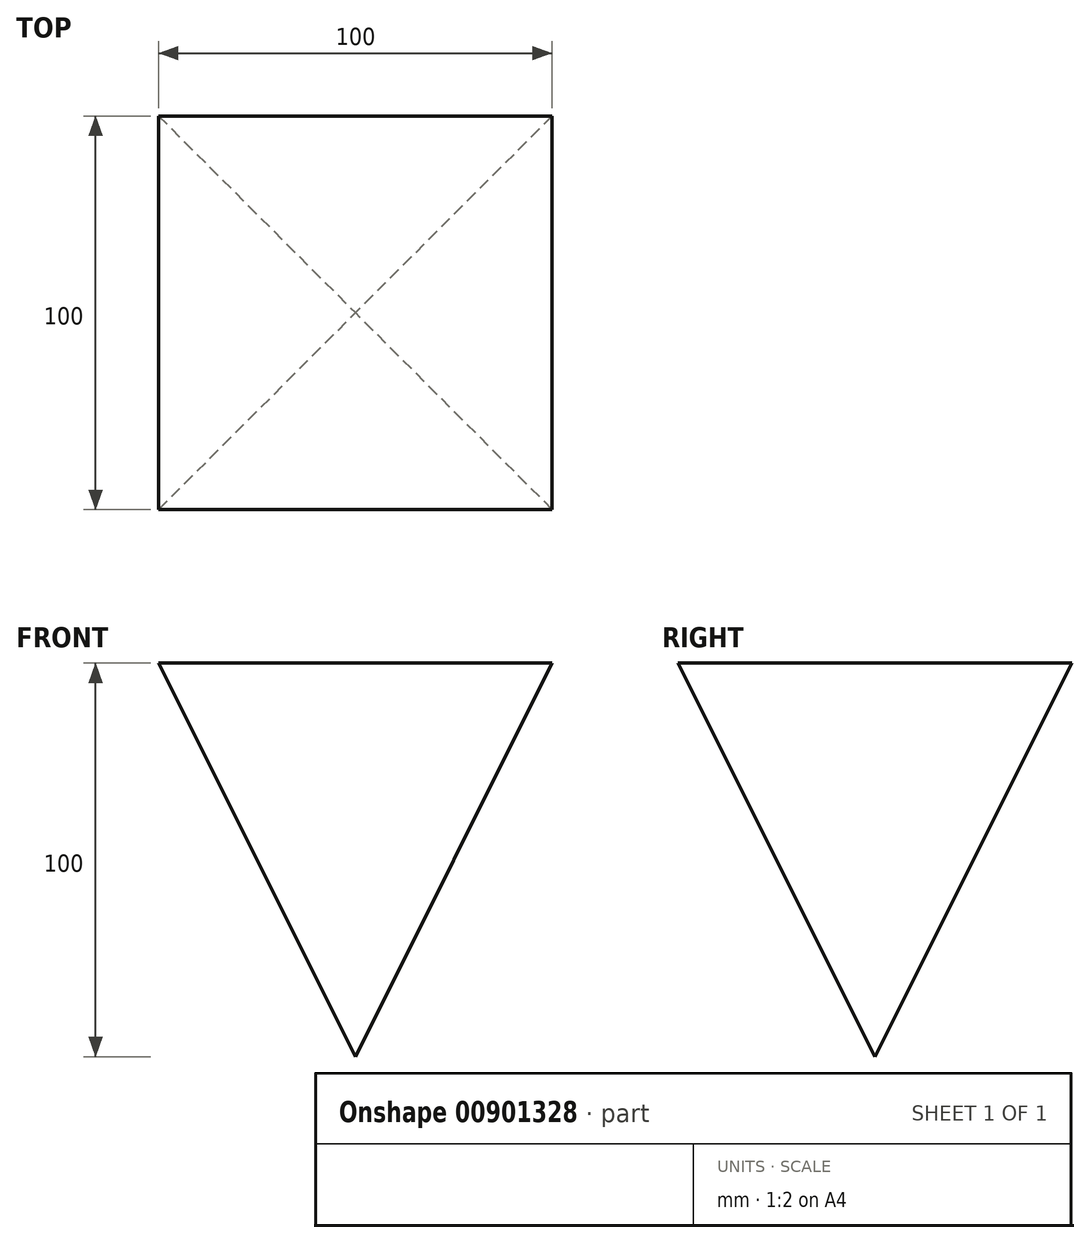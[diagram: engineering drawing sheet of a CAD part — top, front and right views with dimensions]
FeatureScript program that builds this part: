
annotation { "Feature Type Name" : "Feature", "Feature Type Description" : "" }
export const myFeature = defineFeature(function(context is Context, id is Id, definition is map)
    precondition{}
    {
        {
            var Q0;
            Q0=qCreatedBy(makeId("Top.planeOp"),FACE);
            var sketch = newSketch(context, id + "F0", { "sketchPlane" : qUnion([Q0])});
            skLineSegment(sketch, "E0.bottom", {"start": v(-50, 50) * mm, "end": v(50, 50) * mm});
            skLineSegment(sketch, "E0.top", {"start": v(-50, -50) * mm, "end": v(50, -50) * mm});
            skLineSegment(sketch, "E0.left", {"start": v(-50, 50) * mm, "end": v(-50, -50) * mm});
            skLineSegment(sketch, "E0.right", {"start": v(50, 50) * mm, "end": v(50, -50) * mm});
            skSolve(sketch);
        }
        {
            var Q0;
            Q0 = qSketchRegion(id + "F0", true);
            extrude(context, id + "F1", {"entities" : qUnion([Q0]), "endBound" : BoundingType.SYMMETRIC, "depth" : 100 * mm, "offsetDistance" : 25 * mm});
        }
        {
            var Q0;
            Q0=makeQuery(id+"F1.opExtrude","SWEPT_FACE",FACE,{"disambiguationData":[OSD([sQuery(id+"F0.wireOp",EDGE,"E0.right")])]});
            var sketch = newSketch(context, id + "F2", { "sketchPlane" : qUnion([Q0])});
            skLineSegment(sketch, "E1", {"start": v(50, 50) * mm, "end": v(0, -50) * mm});
            skLineSegment(sketch, "E2", {"start": v(-50, 50) * mm, "end": v(0, -50) * mm});
            skLineSegment(sketch, "E3", {"start": v(0, -50) * mm, "end": v(50, -50) * mm});
            skLineSegment(sketch, "E4", {"start": v(50, -50) * mm, "end": v(50, 50) * mm});
            skLineSegment(sketch, "E5", {"start": v(0, -50) * mm, "end": v(-50, -50) * mm});
            skLineSegment(sketch, "E6", {"start": v(-50, -50) * mm, "end": v(-50, 50) * mm});
            skSolve(sketch);
        }
        {
            var Q0;
            Q0=makeQuery(id+"F2.imprint","IMPRINT",FACE,{"disambiguationData":[TD([[makeQuery(id+"F2.imprint","IMPRINT",EDGE,{"derivedFrom":sQuery(id+"F2.wireOp",EDGE,"E2")}),-1.0]])]});
            var Q1;
            Q1=makeQuery(id+"F2.imprint","IMPRINT",FACE,{"disambiguationData":[TD([[makeQuery(id+"F2.imprint","IMPRINT",EDGE,{"derivedFrom":sQuery(id+"F2.wireOp",EDGE,"E1")}),1.0]])]});
            var Q2;
            Q2=makeQuery(id+"F1.opExtrude","SWEPT_FACE",FACE,{"disambiguationData":[OSD([sQuery(id+"F0.wireOp",EDGE,"E0.left")])]});
            extrude(context, id + "F3", {"entities" : qUnion([Q0, Q1]), "operationType" : NewBodyOperationType.REMOVE, "endBound" : BoundingType.UP_TO_SURFACE, "oppositeDirection" : true, "depth" : 25 * mm, "endBoundEntityFace" : qUnion([Q2]), "offsetDistance" : 25 * mm});
        }
        {
            var Q0;
            Q0=qCreatedBy(makeId("Front.planeOp"),FACE);
            var sketch = newSketch(context, id + "F4", { "sketchPlane" : qUnion([Q0])});
            skLineSegment(sketch, "E7", {"start": v(-50, 50) * mm, "end": v(0, -50) * mm});
            skLineSegment(sketch, "E8", {"start": v(50, 50) * mm, "end": v(0, -50) * mm});
            skLineSegment(sketch, "E9", {"start": v(0, -50) * mm, "end": v(-50, -50) * mm});
            skLineSegment(sketch, "E10", {"start": v(-50, -50) * mm, "end": v(-50, 50) * mm});
            skLineSegment(sketch, "E11", {"start": v(0, -50) * mm, "end": v(50, -50) * mm});
            skLineSegment(sketch, "E12", {"start": v(50, -50) * mm, "end": v(50, 50) * mm});
            skSolve(sketch);
        }
        {
            var Q0;
            Q0 = qSketchRegion(id + "F4", true);
            extrude(context, id + "F5", {"entities" : qUnion([Q0]), "operationType" : NewBodyOperationType.REMOVE, "oppositeDirection" : true, "depth" : 100 * mm, "offsetDistance" : 25 * mm, "hasSecondDirection" : true, "secondDirectionOppositeDirection" : false, "secondDirectionDepth" : 100 * mm});
        }
    });
